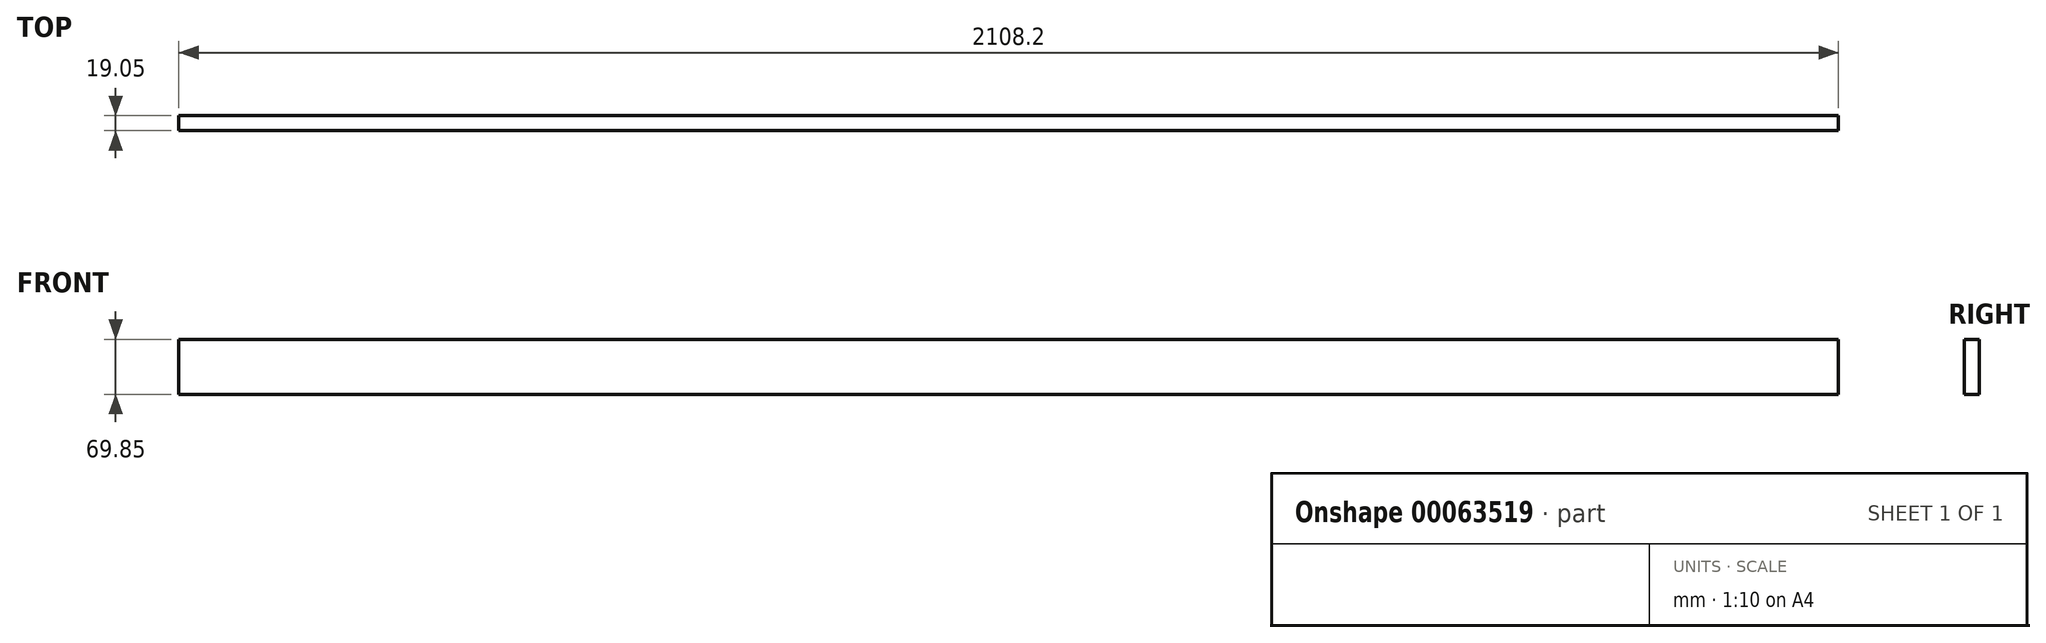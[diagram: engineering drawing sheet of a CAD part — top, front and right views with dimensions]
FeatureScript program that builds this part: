
annotation { "Feature Type Name" : "Feature", "Feature Type Description" : "" }
export const myFeature = defineFeature(function(context is Context, id is Id, definition is map)
    precondition{}
    {
        {
            var Q0;
            Q0=qCreatedBy(makeId("Front.planeOp"),FACE);
            var sketch = newSketch(context, id + "F0", { "sketchPlane" : qUnion([Q0])});
            skLineSegment(sketch, "E0.bottom", {"start": v(-391.07, 59.03) * mm, "end": v(1717.13, 59.03) * mm});
            skLineSegment(sketch, "E0.top", {"start": v(-391.07, -10.82) * mm, "end": v(1717.13, -10.82) * mm});
            skLineSegment(sketch, "E0.left", {"start": v(-391.07, 59.03) * mm, "end": v(-391.07, -10.82) * mm});
            skLineSegment(sketch, "E0.right", {"start": v(1717.13, 59.03) * mm, "end": v(1717.13, -10.82) * mm});
            skSolve(sketch);
        }
        {
            var Q0;
            Q0=makeQuery(id+"F0.imprint","IMPRINT",FACE,{"disambiguationData":[TD([[makeQuery(id+"F0.imprint","IMPRINT",EDGE,{"derivedFrom":sQuery(id+"F0.wireOp",EDGE,"E0.bottom")}),-1.0]])]});
            extrude(context, id + "F1", {"entities" : qUnion([Q0]), "depth" : 19.05 * mm});
        }
    });
